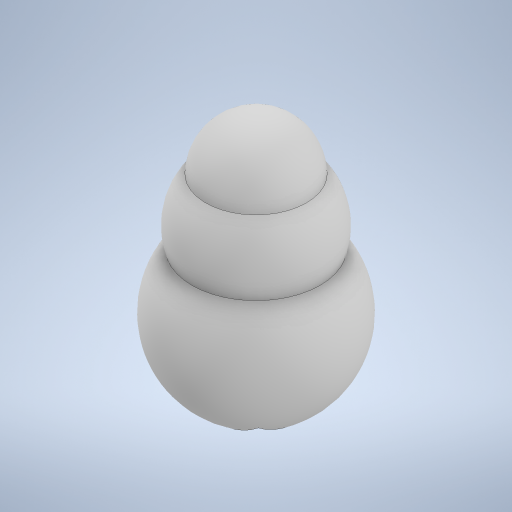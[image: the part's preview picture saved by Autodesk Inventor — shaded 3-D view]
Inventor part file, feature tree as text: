
AUTODESK INVENTOR PART (.ipt)
format: ipt  version: 2024 (Build 280153000, 153)  size: 381,952 bytes
history: native  units: mm
features: sketch x2, revolve x1, extrude x1
ambient origin geometry x8: Origin, YZ Plane, XZ Plane, XY Plane, X Axis, Y Axis, Z Axis, Center Point
bodies: Solid1 (feature_tree)
feature tree (4):
  revolve  "Revolution1"  [1 undecoded]
  extrude  "Extrusion1"  Depth=15.0mm
  sketch  "Sketch1"  dims[d8=25.04mm d9=20.0mm]
  sketch  "Sketch2"  dims[d11=22.0mm d16=15.0mm d18=90.0deg d19=0.0mm d20=0.0mm]
note: 1 required parameter value undecoded (feature->parameter linkage not recoverable at this tier; creation-order binding heuristic only, values carry confidence <= 0.55)
